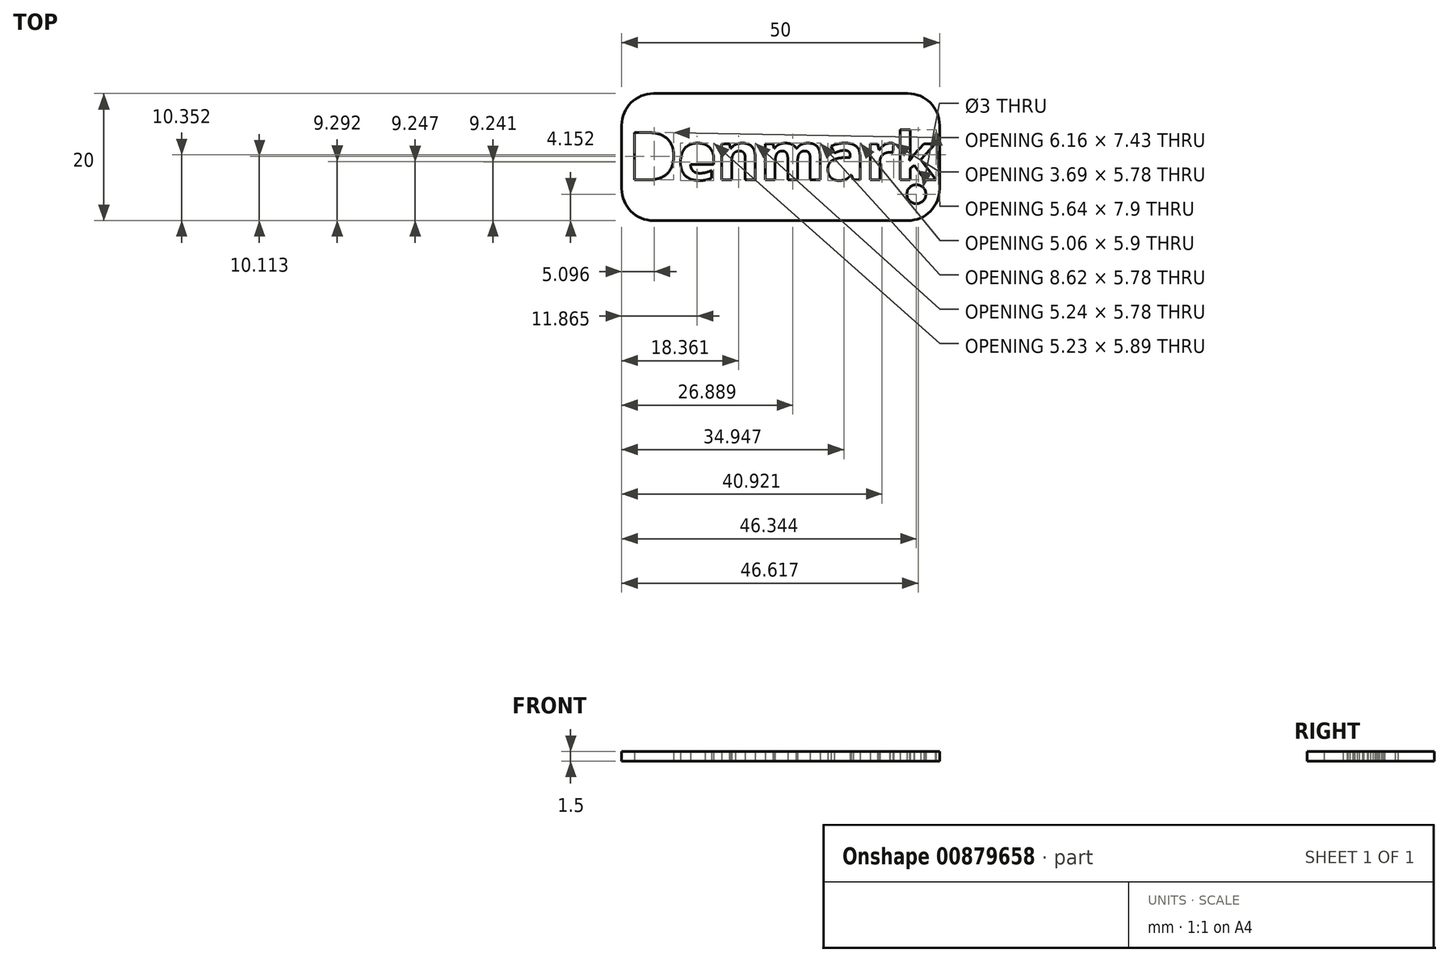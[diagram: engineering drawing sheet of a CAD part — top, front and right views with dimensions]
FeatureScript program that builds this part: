
annotation { "Feature Type Name" : "Feature", "Feature Type Description" : "" }
export const myFeature = defineFeature(function(context is Context, id is Id, definition is map)
    precondition{}
    {
        {
            var Q0;
            Q0=qCreatedBy(makeId("Top.planeOp"),FACE);
            var sketch = newSketch(context, id + "F0", { "sketchPlane" : qUnion([Q0])});
            skLineSegment(sketch, "E0.bottom", {"start": v(25, -10) * mm, "end": v(-25, -10) * mm});
            skLineSegment(sketch, "E0.top", {"start": v(25, 10) * mm, "end": v(-25, 10) * mm});
            skLineSegment(sketch, "E0.left", {"start": v(25, -10) * mm, "end": v(25, 10) * mm});
            skLineSegment(sketch, "E0.right", {"start": v(-25, -10) * mm, "end": v(-25, 10) * mm});
            skPoint(sketch, "E0.middle", {"position": v(0, 0) * mm});
            skCircle(sketch, "E1", {"center": v(21.34, -5.85) * mm, "radius": 1.5 * mm});
            skText(sketch, "E2", { "text": "Denmark", "fontName": "OpenSans-Bold.ttf"});
            const initialGuessF0  = {"E2": [-0.02392, -0.0036, 1, 0, 0.00749]};
            skSetInitialGuess(sketch, initialGuessF0);
            skSolve(sketch);
        }
        {
            var Q0;
            Q0=makeQuery(id+"F0.imprint","IMPRINT",FACE,{"disambiguationData":[TD([[makeQuery(id+"F0.imprint","IMPRINT",EDGE,{"derivedFrom":sQuery(id+"F0.wireOp",EDGE,"E0.bottom")}),-1.0]])]});
            extrude(context, id + "F1", {"entities" : qUnion([Q0]), "depth" : 1.5 * mm, "offsetDistance" : 25 * mm});
        }
        {
            var Q0;
            Q0=makeQuery(id+"F1.opExtrude","SWEPT_EDGE",EDGE,{"disambiguationData":[OSD([sQuery(id+"F0.wireOp",EDGE,"E0.bottom"),sQuery(id+"F0.wireOp",EDGE,"E0.right")])]});
            var Q1;
            Q1=makeQuery(id+"F1.opExtrude","SWEPT_EDGE",EDGE,{"disambiguationData":[OSD([sQuery(id+"F0.wireOp",EDGE,"E0.top"),sQuery(id+"F0.wireOp",EDGE,"E0.right")])]});
            var Q2;
            Q2=makeQuery(id+"F1.opExtrude","SWEPT_EDGE",EDGE,{"disambiguationData":[OSD([sQuery(id+"F0.wireOp",EDGE,"E0.top"),sQuery(id+"F0.wireOp",EDGE,"E0.left")])]});
            var Q3;
            Q3=makeQuery(id+"F1.opExtrude","SWEPT_EDGE",EDGE,{"disambiguationData":[OSD([sQuery(id+"F0.wireOp",EDGE,"E0.bottom"),sQuery(id+"F0.wireOp",EDGE,"E0.left")])]});
            fillet(context, id + "F2", {"entities" : qUnion([Q0, Q1, Q2, Q3]), "radius" : 5 * mm, "tangentPropagation" : true, "allowEdgeOverflow" : false});
        }
    });
